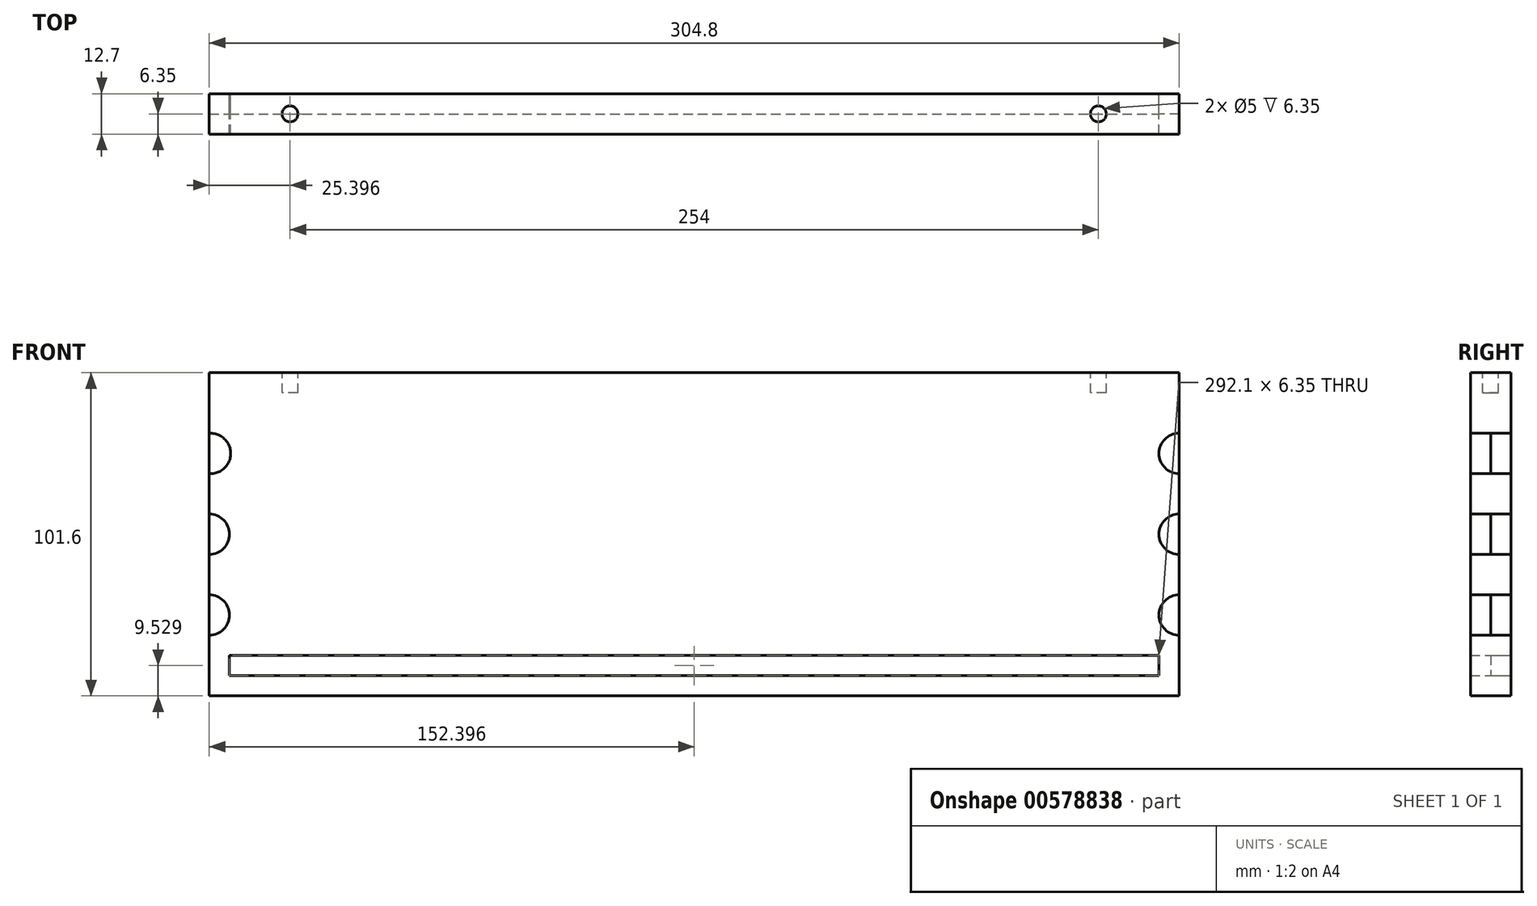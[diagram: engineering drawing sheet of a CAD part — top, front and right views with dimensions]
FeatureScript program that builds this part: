
annotation { "Feature Type Name" : "Feature", "Feature Type Description" : "" }
export const myFeature = defineFeature(function(context is Context, id is Id, definition is map)
    precondition{}
    {
        {
            var Q0;
            Q0=qCreatedBy(makeId("Front.planeOp"),FACE);
            var sketch = newSketch(context, id + "F0", { "sketchPlane" : qUnion([Q0])});
            skLineSegment(sketch, "E0.bottom", {"start": v(-88.31, 66.7) * mm, "end": v(216.49, 66.7) * mm});
            skLineSegment(sketch, "E0.top", {"start": v(-88.31, -34.9) * mm, "end": v(216.49, -34.9) * mm});
            skLineSegment(sketch, "E0.left", {"start": v(-88.31, 66.7) * mm, "end": v(-88.31, -34.9) * mm});
            skLineSegment(sketch, "E0.right", {"start": v(216.49, 66.7) * mm, "end": v(216.49, -34.9) * mm});
            skArc(sketch, "E1", {"start": v(-88.31, 34.94) * mm, "mid": v(-81.56, 41.3) * mm, "end": v(-88.31, 47.64) * mm});
            skArc(sketch, "E2", {"start": v(-88.31, 9.54) * mm, "mid": v(-81.96, 15.9) * mm, "end": v(-88.31, 22.24) * mm});
            skArc(sketch, "E3", {"start": v(-88.31, -15.86) * mm, "mid": v(-81.96, -9.5) * mm, "end": v(-88.31, -3.16) * mm});
            skArc(sketch, "E4", {"start": v(216.49, 47.64) * mm, "mid": v(210.14, 41.3) * mm, "end": v(216.49, 34.94) * mm});
            skArc(sketch, "E5", {"start": v(216.49, 22.24) * mm, "mid": v(210.14, 15.9) * mm, "end": v(216.49, 9.54) * mm});
            skArc(sketch, "E6", {"start": v(216.49, -3.16) * mm, "mid": v(210.14, -9.5) * mm, "end": v(216.49, -15.86) * mm});
            skLineSegment(sketch, "E7.bottom", {"start": v(-81.96, -22.2) * mm, "end": v(210.14, -22.2) * mm});
            skLineSegment(sketch, "E7.top", {"start": v(-81.96, -28.56) * mm, "end": v(210.14, -28.56) * mm});
            skLineSegment(sketch, "E7.left", {"start": v(-81.96, -22.2) * mm, "end": v(-81.96, -28.56) * mm});
            skLineSegment(sketch, "E7.right", {"start": v(210.14, -22.2) * mm, "end": v(210.14, -28.56) * mm});
            skSolve(sketch);
        }
        {
            var Q0;
            Q0=makeQuery(id+"F0.imprint","IMPRINT",FACE,{"disambiguationData":[TD([[makeQuery(id+"F0.imprint","IMPRINT",EDGE,{"derivedFrom":sQuery(id+"F0.wireOp",EDGE,"E7.bottom")}),-1.0]])]});
            extrude(context, id + "F1", {"entities" : qUnion([Q0]), "depth" : 6.35 * mm, "offsetDistance" : 25.4 * mm});
        }
        {
            var Q0;
            {var subQ0=sQuery(id+"F0.wireOp",EDGE,"E3");Q0=makeQuery(id+"F0.imprint","IMPRINT",FACE,{"disambiguationData":[TD([[makeQuery(id+"F0.imprint","IMPRINT",EDGE,{"derivedFrom":subQ0}),1.0]])]});}
            var Q1;
            {var subQ0=sQuery(id+"F0.wireOp",EDGE,"E2");Q1=makeQuery(id+"F0.imprint","IMPRINT",FACE,{"disambiguationData":[TD([[makeQuery(id+"F0.imprint","IMPRINT",EDGE,{"derivedFrom":subQ0}),1.0]])]});}
            var Q2;
            {var subQ0=sQuery(id+"F0.wireOp",EDGE,"E1");Q2=makeQuery(id+"F0.imprint","IMPRINT",FACE,{"disambiguationData":[TD([[makeQuery(id+"F0.imprint","IMPRINT",EDGE,{"derivedFrom":subQ0}),1.0]])]});}
            var Q3;
            {var subQ0=sQuery(id+"F0.wireOp",EDGE,"E4");Q3=makeQuery(id+"F0.imprint","IMPRINT",FACE,{"disambiguationData":[TD([[makeQuery(id+"F0.imprint","IMPRINT",EDGE,{"derivedFrom":subQ0}),1.0]])]});}
            var Q4;
            {var subQ0=sQuery(id+"F0.wireOp",EDGE,"E5");Q4=makeQuery(id+"F0.imprint","IMPRINT",FACE,{"disambiguationData":[TD([[makeQuery(id+"F0.imprint","IMPRINT",EDGE,{"derivedFrom":subQ0}),1.0]])]});}
            var Q5;
            {var subQ0=sQuery(id+"F0.wireOp",EDGE,"E6");Q5=makeQuery(id+"F0.imprint","IMPRINT",FACE,{"disambiguationData":[TD([[makeQuery(id+"F0.imprint","IMPRINT",EDGE,{"derivedFrom":subQ0}),1.0]])]});}
            extrude(context, id + "F2", {"entities" : qUnion([Q0, Q1, Q2, Q3, Q4, Q5]), "depth" : 6.35 * mm, "offsetDistance" : 25.4 * mm});
        }
        {
            var Q0;
            {var subQ1=sQuery(id+"F0.wireOp",EDGE,"E0.bottom");Q0=makeQuery(id+"F0.imprint","IMPRINT",FACE,{"disambiguationData":[TD([[makeQuery(id+"F0.imprint","IMPRINT",EDGE,{"derivedFrom":subQ1}),-1.0]])]});}
            var Q1;
            Q1=makeQuery(id+"F2.opExtrude","SWEPT_BODY",BODY,{"disambiguationData":[OSD([sQuery(id+"F0.wireOp",EDGE,"E0.right"),sQuery(id+"F0.wireOp",EDGE,"E4")])]});
            extrude(context, id + "F3", {"entities" : qUnion([Q0]), "depth" : 12.7 * mm, "endBoundEntityBody" : qUnion([Q1]), "offsetDistance" : 25.4 * mm});
        }
        {
            var Q0;
            Q0=makeQuery(id+"F3.opExtrude","SWEPT_FACE",FACE,{"disambiguationData":[OSD([sQuery(id+"F0.wireOp",EDGE,"E0.bottom")])]});
            var sketch = newSketch(context, id + "F4", { "sketchPlane" : qUnion([Q0])});
            skCircle(sketch, "E8", {"center": v(-62.91, -6.35) * mm, "radius": 2.5 * mm});
            skCircle(sketch, "E9", {"center": v(191.09, -6.35) * mm, "radius": 2.5 * mm});
            skSolve(sketch);
        }
        {
            var Q0;
            Q0=makeQuery(id+"F4.imprint","IMPRINT",FACE,{"disambiguationData":[TD([[makeQuery(id+"F4.imprint","IMPRINT",EDGE,{"derivedFrom":sQuery(id+"F4.wireOp",EDGE,"E9")}),1.0]])]});
            var Q1;
            Q1=makeQuery(id+"F4.imprint","IMPRINT",FACE,{"disambiguationData":[TD([[makeQuery(id+"F4.imprint","IMPRINT",EDGE,{"derivedFrom":sQuery(id+"F4.wireOp",EDGE,"E8")}),1.0]])]});
            extrude(context, id + "F5", {"entities" : qUnion([Q0, Q1]), "operationType" : NewBodyOperationType.REMOVE, "oppositeDirection" : true, "depth" : 6.35 * mm, "offsetDistance" : 25.4 * mm});
        }
    });
